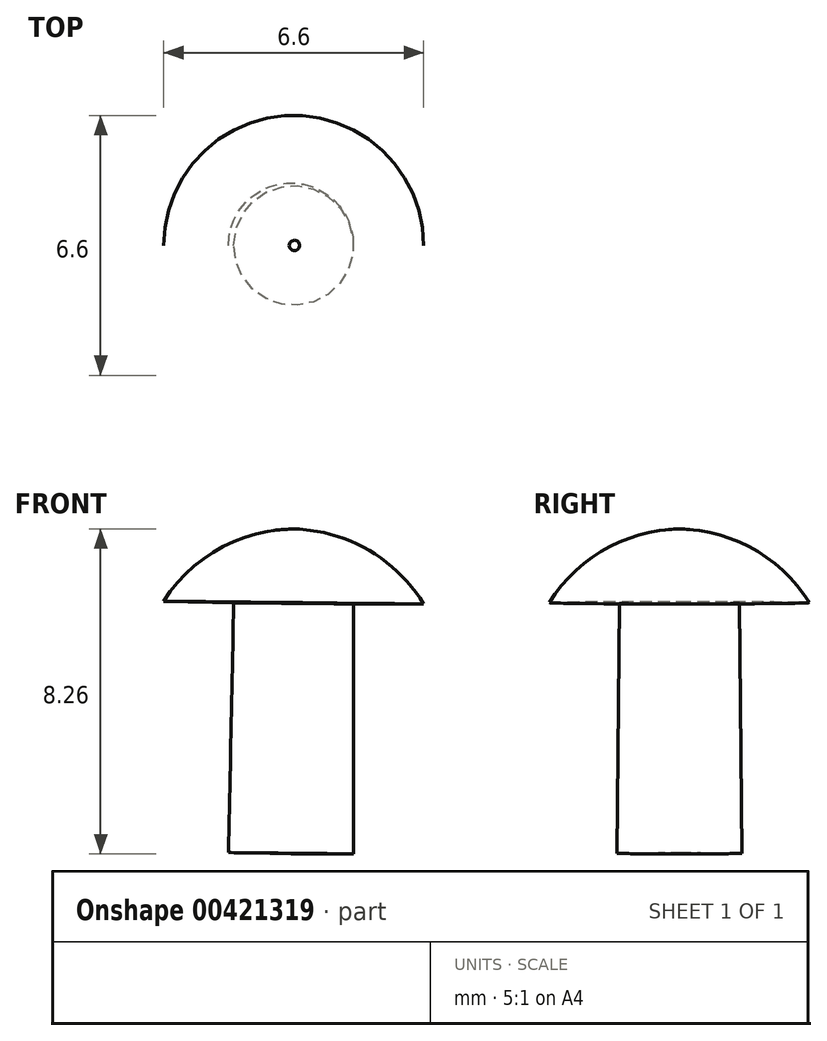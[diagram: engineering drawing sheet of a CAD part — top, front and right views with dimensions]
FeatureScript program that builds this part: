
annotation { "Feature Type Name" : "Feature", "Feature Type Description" : "" }
export const myFeature = defineFeature(function(context is Context, id is Id, definition is map)
    precondition{}
    {
        {
            var Q0;
            Q0=qCreatedBy(makeId("Front.planeOp"),FACE);
            var sketch = newSketch(context, id + "F0", { "sketchPlane" : qUnion([Q0])});
            skLineSegment(sketch, "E0", {"start": v(8.7, 0.62) * mm, "end": v(10.29, 0.62) * mm});
            skLineSegment(sketch, "E1", {"start": v(10.29, 0.62) * mm, "end": v(10.29, 6.97) * mm});
            skLineSegment(sketch, "E2", {"start": v(10.29, 6.97) * mm, "end": v(12.07, 6.97) * mm});
            skArc(sketch, "E3", {"start": v(12.07, 6.97) * mm, "mid": v(10.67, 8.34) * mm, "end": v(8.79, 8.88) * mm});
            skLineSegment(sketch, "E4", {"start": v(8.7, 0.62) * mm, "end": v(8.79, 8.88) * mm});
            skSolve(sketch);
        }
        {
            var Q0;
            Q0=makeQuery(id+"F0.imprint","IMPRINT",FACE,{"disambiguationData":[TD([[makeQuery(id+"F0.imprint","IMPRINT",EDGE,{"derivedFrom":sQuery(id+"F0.wireOp",EDGE,"E0")}),1.0]])]});
            var Q1;
            Q1=sQuery(id+"F0.wireOp",EDGE,"E4");
            revolve(context, id + "F1", {"entities" : qUnion([Q0]), "axis" : qUnion([Q1]), "revolveType" : RevolveType.FULL});
        }
    });
